# Revit family: Toilet_Seat-Square_Closed_Front-KOHLER-REPLAY-K-23107IN
name_source: partatom
category: Specialty Equipment
units: mm (PartAtom-declared; Revit-internal decimal feet)

## family parameters
Cut with Voids When Loaded = No
Host = Face
OmniClass Number = 23.31.19.19.17
OmniClass Title = Water Closet Seats
Part Type = Normal
Room Calculation Point = No
Round Connector Dimension = Use Diameter
Shared = No

## types (3) — shared parameters
ADA Compliant = No
Assembly Code = C1030200
Date Modified = 05/21/2024
Default Elevation = 15"
Description = Quiet-close square-front toilet seat
Height = 2 5/16"
Length = 17 1/2"
Manufacturer = Kohler Co.
Master Format 2014 = 10 28 00
Master Format 2014 Name = Toilet, Bath, and Laundry Accessories
Material = Plastic
Product Name = Replay
URL = https://www.kohler.co.in
WaterSense Certified = No
Width = 14 3/8"

## per-type parameters (varying)
| type | Finish | Model | Product Page URL | Type |
| 0-White | Kohler-Plastic-0-White | K-23107IN-UF-0 | https://www.kohler.co.in | 1 |
| 58-Thunder Grey | Kohler-Plastic-58-Thunder_Grey | K-23107IN-UF-58 |  | 2 |
| K4-Cashmere | Kohler-Plastic-K4-Cashmere | K-23107IN-UF-K4 |  | 3 |

## geometry (parser evidence)
native form markers: Sweep x4
no freeform markers — native parametric forms only
